# Revit family: ALBA_R68ExWS930xx
name_source: partatom
category: Leuchten
units: mm (PartAtom-declared; Revit-internal decimal feet)

## family parameters
Basisbauteil = Fläche
Beim Laden mit Abzugskörper schneiden = Nein
Bemaßung runder Anschluss = Durchmesser verwenden
Gemeinsam genutzt = Nein
Lichtquelle = Ja
OmniClass-Nummer = 23.80.70.11
OmniClass-Titel = Luminaries for Internal Lighting
Raumberechnungspunkt = Nein
Teiletyp = Normal

## types (6) — shared parameters
Baugruppenkennzeichen = D5020200
Emissionsform beim Rendern sichtbar = Nein
Farbfilter = 16777215
Farbtemperaturverschiebung bei Dämpfen der Lampe = <Keine Auswahl>
Hersteller = RIDI Leuchten GmbH
Lampe = LED
Neigungswinkel = 90.00°
Scheinlast = 8 VA
URL = www.ridi.de
Von Kreisdurchmesser aussenden = 54 mm  [stored 0.177165 ft]
brand = RIDI
conformity mark = CE
electrical safety class = 2
height = 67 mm
ingress protection (IP) code = IP20
length = 72 mm  [stored 0.23622 ft]
nominal frequency = 50-60Hz
nominal voltage = 230
rated input power = 8
voltage type (AC, DC, UC) = AC
weight = 0.34 kg
width = 72 mm  [stored 0.23622 ft]
zero-valued in all types: Vorgabe-Ansicht

## per-type parameters (varying)
| type | Datei für fotometrisches Netz | Modell |
| ALBA R68E NDWS930SF0080OS | Master_ALBA_R68E_NDWS840_Diffusor.IES | 0322104 |
| ALBA R68E NDWS930S0080 | Master_ALBA_R68E_NDWS840_Linse_S.IES | 0322105 |
| ALBA R68E NDWS930S0080J | Master_ALBA_R68E_NDWS840_Linse_S.IES | 0322106 |
| ALBA R68E DAWS930SF0080OS | Master_ALBA_R68E_NDWS840_Diffusor.IES | 0332104 |
| ALBA R68E DAWS930S0080 | Master_ALBA_R68E_NDWS840_Linse_S.IES | 0332105 |
| ALBA R68E DAWS930S0080J | Master_ALBA_R68E_NDWS840_Linse_S.IES | 0332106 |

note: column(s) folded — value = type name in every type: product name

note: [stored X ft] marks values corroborated as IEEE doubles in the binary element streams (Revit-internal decimal feet)
